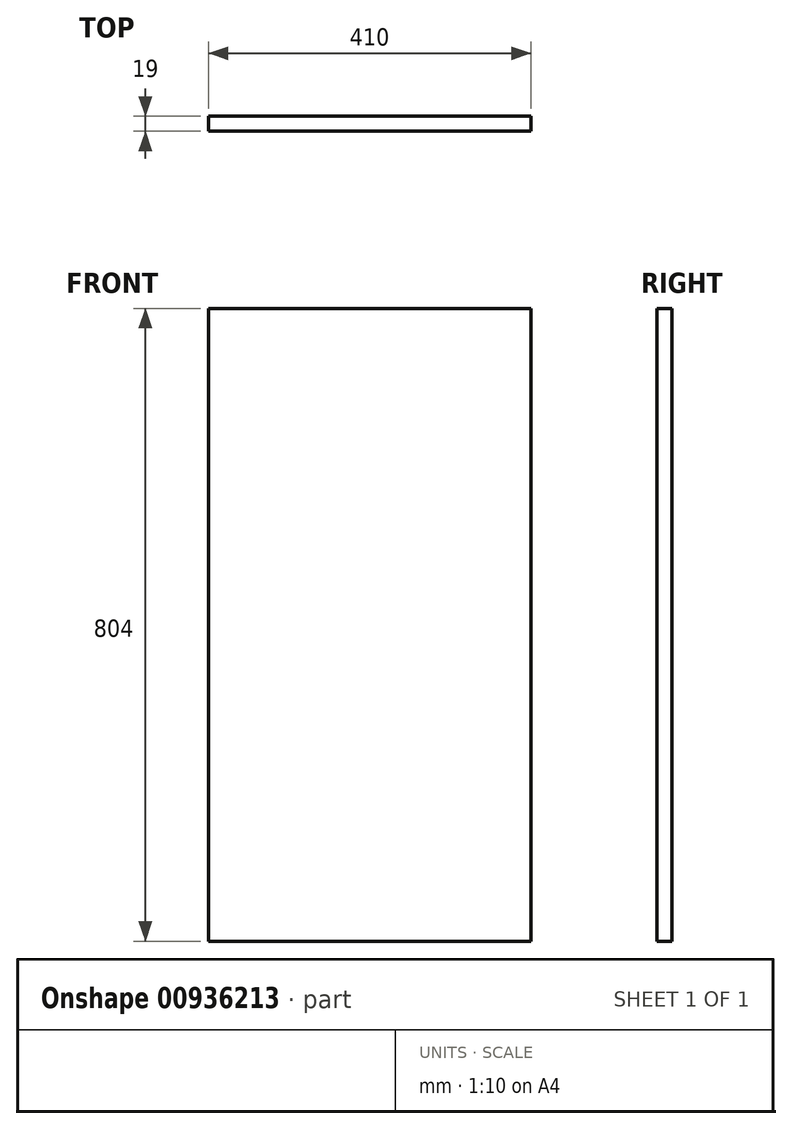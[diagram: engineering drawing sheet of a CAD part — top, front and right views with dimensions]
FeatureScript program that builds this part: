
annotation { "Feature Type Name" : "Feature", "Feature Type Description" : "" }
export const myFeature = defineFeature(function(context is Context, id is Id, definition is map)
    precondition{}
    {
        {
            var Q0;
            Q0=qCreatedBy(makeId("Front.planeOp"),FACE);
            var sketch = newSketch(context, id + "F0", { "sketchPlane" : qUnion([Q0])});
            skLineSegment(sketch, "E0.bottom", {"start": v(0, 0) * mm, "end": v(410, 0) * mm});
            skLineSegment(sketch, "E0.top", {"start": v(0, 804) * mm, "end": v(410, 804) * mm});
            skLineSegment(sketch, "E0.left", {"start": v(0, 0) * mm, "end": v(0, 804) * mm});
            skLineSegment(sketch, "E0.right", {"start": v(410, 0) * mm, "end": v(410, 804) * mm});
            skSolve(sketch);
        }
        {
            var Q0;
            Q0=makeQuery(id+"F0.imprint","IMPRINT",FACE,{"disambiguationData":[TD([[makeQuery(id+"F0.imprint","IMPRINT",EDGE,{"derivedFrom":sQuery(id+"F0.wireOp",EDGE,"E0.bottom")}),1.0]])]});
            extrude(context, id + "F1", {"entities" : qUnion([Q0]), "depth" : 19 * mm, "offsetDistance" : 25 * mm});
        }
    });
